# Revit family: VIESSMANN - Vitocrossal 200 CM2C
name_source: partatom
category: Wyposażenie mechaniczne
revit_build: Autodesk Revit 2017 (Build: 20160720_1515(x64)
units: mm (PartAtom-declared; Revit-internal decimal feet)

## family parameters
Numer OmniClass = 23.15.30.27.21
Oparty na płaszczyźnie roboczej = Nie
Punkt obliczania pomieszczeń = Nie
Tnij formami wycięć po wczytaniu = Tak
Typ części = Normalny
Tytuł OmniClass = Gas Tanks and Gasholders
Współdzielony = Nie
Wymiar okrągłego złącza = Użyj średnicy
Zawsze pionowo = Tak

## types (7) — shared parameters
Autor = https://www.archispace.pl
Ciśnienie kontrolne = 0.8 MPa
Ciśnienie na przyłączu gazu - gaz płynny = 5 - 5.75 kPa
Ciśnienie na przyłączu gazu - gaz ziemny = 2 - 5 kPa
Częstotliwość = 50 Hz
Dop. maks. ciśnienie robocze = 0.6 MPa
Dop. min. ciśnienie robocze = 0.1 MPa
Dop. temperatura na zasilaniu (=temperatura progowa) = 110 °C
Dop. temperatura robocza = 95 °C
Długość = 1755 mm  [stored 5.75787 ft]
Długość fundamentu = 1200 mm
Długość palnika = 435 mm  [stored 1.42717 ft]
Liczba biegunów = 1
NOx = Klasa 6, <56 mg/kWh
Napięcie zasilania = 230 V
Numer identyfikacyjny produktu = CE-0085CR0391
Odsunięcie króćca powrotu do kotła = 280 mm  [stored 0.918635 ft]
Opis = Gazowy kocioł grzewczy
Opis indeksowy = CE-0085CR0391
Opory przepływu = 0.0 MPa
PN 6 DN - Przyłącze zabezpieczające = 50.00 mm
Parametry produktu wg. EnEV - sprawność znormalizowana przy temperaturze w systemie grzewczym wyn. 40/30°C = do 98 (Hs)
Parametry produktu wg. EnEV - sprawność znormalizowana przy temperaturze w systemie grzewczym wyn. 75/60°C = do 96 (Hs)
Parametry spalin - dyspozycyjne ciśnienie tłoczenia na króćcu spalin = 0.0 MPa
Parametry spalin - przy obciążeniu częściowym (przy temp. wody na powrocie wyn. 30°C) = 35 °C
Parametry spalin - przy znamionowej mocy cieplnej (przy temp. wody na powrocie wyn. 30°C) = 45 °C
Parametry spalin - przy znamionowej mocy cieplnej (przy temp. wody na powrocie wyn. 60°C) = 75 °C
Producent = Viessmann Sp.z.o.o.
Przyłącze powietrza do spalania z zewnątrz (opcja dodatkowa) = 80 mm  [stored 0.262467 ft]
Spust = 1"
Syfon z odpływem kondensatu = 20.00 mm
Szerokość fundamentu = 800 mm  [stored 2.62467 ft]
Szerokość palnika = 546 mm  [stored 1.79134 ft]
Typ palnika = CM2C
URL = https://www.viessmann-projektant.pl
Viessmann Kolor 1 = Viessmann Kolor 1
Viessmann Kolor 2 = Viessmann Kolor 2
Viessmann Kolor 3 = Viessmann Kolor 3
Współczynnik mocy = 1
Wykonanie palnika = Wbudowany Modulowany
Wysokość fundamentu = 100 mm  [stored 0.328084 ft]
Zawór bezpieczeństwa (gwint zewnętrzny) = 1 1/4"

## per-type parameters (varying)
- CM2C 87kW: Długość całkowita palnika=623 mm  [stored 2.04396 ft]; Długość podstawy=1073 mm  [stored 3.52034 ft]; Masa - palnik z armaturą uniwersalną i pokrywą palnika=35.70 kg; Masa całkowita=348.00 kg; Masa znamionowa (=zezwolenie)=202.00 kg; Moc cieplna palnika dolna=27 kW; Moc cieplna palnika górna=82 kW; Moc nominalna=87 kW; Model=Gazowy kocioł kondensacyjny Viessmann Vitocrossal CM2C 87kW / Gas condensing boiler Viessmann Vitocrossal CM2C 87kW; Odsunięcie króćca przyłącza zabezpieczającego=537 mm  [stored 1.76181 ft]; Odsunięcie króćca zasilania z kotła=737 mm  [stored 2.41798 ft]; Odsunięcie podstawy=455 mm; PN 6 DN - powrót do kotła=50 mm  [stored 0.164042 ft]; PN 6 DN - zasilanie z kotła=50 mm  [stored 0.164042 ft]; Parametry spalin - masowe natężenie przepływu w przypadku gazu ziemnego przy obciążeniu częściowym=42 kg/h; Parametry spalin - masowe natężenie przepływu w przypadku gazu ziemnego przy znamionowej mocy cieplnej=126 kg/h; Pobór mocy elektrycznej - przy dolnej mocy cieplnej=23 W; Pobór mocy elektrycznej - przy górnej mocy cieplnej=75 W; Pojemność wodna kotła=225.0 L; Przepływ maksymalny=3.76 m³/h; Przyłącze gazu=1"; Przyłącze spalin=160 mm  [stored 0.524934 ft]; Straty energii dyżurnej qB,70=0.6 %; Szerokość=810 mm  [stored 2.65748 ft]; Szerokość podstawy=660 mm  [stored 2.16535 ft]; Wartości na przyłączu (w odniesieniu do maks. obciążenia) - gaz ziemny GZ-50/G20=2.8 - 8.7 m3/h; Wartości na przyłączu (w odniesieniu do maks. obciążenia) - gaz ziemny GZ41,5/G27=3.3 - 10.1 m3/h; Wysokość=1114 mm  [stored 3.65486 ft]; Wysokość do króćców=1178 mm; Wysokość króćca spalin=539 mm  [stored 1.76837 ft]; Wysokość palnika=514 mm  [stored 1.68635 ft]; Występ króćca spalin=19 mm  [stored 0.062336 ft]; Zakres znamionowej mocy cieplnej przy Tv/Tr 50/30°C=29 - 87; Zakres znamionowej mocy cieplnej przy Tv/Tr 80/60°C=26 - 80; Znamionowe obciążenie cieplne=82 kW
- CM2C 115kW: Długość całkowita palnika=623 mm  [stored 2.04396 ft]; Długość podstawy=1073 mm  [stored 3.52034 ft]; Masa - palnik z armaturą uniwersalną i pokrywą palnika=41.00 kg; Masa całkowita=350.00 kg; Masa znamionowa (=zezwolenie)=204.00 kg; Moc cieplna palnika dolna=36 kW; Moc cieplna palnika górna=109 kW; Moc nominalna=115 kW; Model=Gazowy kocioł kondensacyjny Viessmann Vitocrossal CM2C 115kW / Gas condensing boiler Viessmann Vitocrossal CM2C 115kW; Odsunięcie króćca przyłącza zabezpieczającego=537 mm  [stored 1.76181 ft]; Odsunięcie króćca zasilania z kotła=737 mm  [stored 2.41798 ft]; Odsunięcie podstawy=455 mm; PN 6 DN - powrót do kotła=50 mm  [stored 0.164042 ft]; PN 6 DN - zasilanie z kotła=50 mm  [stored 0.164042 ft]; Parametry spalin - masowe natężenie przepływu w przypadku gazu ziemnego przy obciążeniu częściowym=56 kg/h; Parametry spalin - masowe natężenie przepływu w przypadku gazu ziemnego przy znamionowej mocy cieplnej=166 kg/h; Pobór mocy elektrycznej - przy dolnej mocy cieplnej=43 W; Pobór mocy elektrycznej - przy górnej mocy cieplnej=140 W; Pojemność wodna kotła=225.0 L; Przepływ maksymalny=4.97 m³/h; Przyłącze gazu=1"; Przyłącze spalin=160 mm  [stored 0.524934 ft]; Straty energii dyżurnej qB,70=0.5 %; Szerokość=810 mm  [stored 2.65748 ft]; Szerokość podstawy=660 mm  [stored 2.16535 ft]; Wartości na przyłączu (w odniesieniu do maks. obciążenia) - gaz ziemny GZ-50/G20=3.8 - 11.5 m3/h; Wartości na przyłączu (w odniesieniu do maks. obciążenia) - gaz ziemny GZ41,5/G27=4.4 - 13.3 m3/h; Wysokość=1114 mm  [stored 3.65486 ft]; Wysokość do króćców=1178 mm; Wysokość króćca spalin=539 mm  [stored 1.76837 ft]; Wysokość palnika=514 mm  [stored 1.68635 ft]; Występ króćca spalin=19 mm  [stored 0.062336 ft]; Zakres znamionowej mocy cieplnej przy Tv/Tr 50/30°C=38 - 115; Zakres znamionowej mocy cieplnej przy Tv/Tr 80/60°C=35 - 105; Znamionowe obciążenie cieplne=109 kW
- CM2C 142kW: Długość całkowita palnika=623 mm  [stored 2.04396 ft]; Długość podstawy=1073 mm  [stored 3.52034 ft]; Masa - palnik z armaturą uniwersalną i pokrywą palnika=41.00 kg; Masa całkowita=351.00 kg; Masa znamionowa (=zezwolenie)=205.00 kg; Moc cieplna palnika dolna=45 kW; Moc cieplna palnika górna=134 kW; Moc nominalna=142 kW; Model=Gazowy kocioł kondensacyjny Viessmann Vitocrossal CM2C 142kW / Gas condensing boiler Viessmann Vitocrossal CM2C 142kW; Odsunięcie króćca przyłącza zabezpieczającego=537 mm  [stored 1.76181 ft]; Odsunięcie króćca zasilania z kotła=737 mm  [stored 2.41798 ft]; Odsunięcie podstawy=455 mm; PN 6 DN - powrót do kotła=50 mm  [stored 0.164042 ft]; PN 6 DN - zasilanie z kotła=50 mm  [stored 0.164042 ft]; Parametry spalin - masowe natężenie przepływu w przypadku gazu ziemnego przy obciążeniu częściowym=69 kg/h; Parametry spalin - masowe natężenie przepływu w przypadku gazu ziemnego przy znamionowej mocy cieplnej=207 kg/h; Pobór mocy elektrycznej - przy dolnej mocy cieplnej=50 W; Pobór mocy elektrycznej - przy górnej mocy cieplnej=210 W; Pojemność wodna kotła=221.0 L; Przepływ maksymalny=6.13 m³/h; Przyłącze gazu=1"; Przyłącze spalin=160 mm  [stored 0.524934 ft]; Straty energii dyżurnej qB,70=0.4 %; Szerokość=810 mm  [stored 2.65748 ft]; Szerokość podstawy=660 mm  [stored 2.16535 ft]; Wartości na przyłączu (w odniesieniu do maks. obciążenia) - gaz ziemny GZ-50/G20=4.7 - 14.2 m3/h; Wartości na przyłączu (w odniesieniu do maks. obciążenia) - gaz ziemny GZ41,5/G27=5.5 - 16.5 m3/h; Wysokość=1114 mm  [stored 3.65486 ft]; Wysokość do króćców=1178 mm; Wysokość króćca spalin=539 mm  [stored 1.76837 ft]; Wysokość palnika=514 mm  [stored 1.68635 ft]; Występ króćca spalin=19 mm  [stored 0.062336 ft]; Zakres znamionowej mocy cieplnej przy Tv/Tr 50/30°C=47 - 142; Zakres znamionowej mocy cieplnej przy Tv/Tr 80/60°C=43 - 130; Znamionowe obciążenie cieplne=134 kW
- CM2C 75kW: Długość całkowita palnika=623 mm  [stored 2.04396 ft]; Długość podstawy=1073 mm  [stored 3.52034 ft]; Masa - palnik z armaturą uniwersalną i pokrywą palnika=35.70 kg; Masa całkowita=348.00 kg; Masa znamionowa (=zezwolenie)=202.00 kg; Moc cieplna palnika dolna=27 kW; Moc cieplna palnika górna=71 kW; Moc nominalna=75 kW; Model=Gazowy kocioł kondensacyjny Viessmann Vitocrossal CM2C 75kW / Gas condensing boiler Viessmann Vitocrossal CM2C 75kW; Odsunięcie króćca przyłącza zabezpieczającego=537 mm  [stored 1.76181 ft]; Odsunięcie króćca zasilania z kotła=737 mm  [stored 2.41798 ft]; Odsunięcie podstawy=455 mm; PN 6 DN - powrót do kotła=50 mm  [stored 0.164042 ft]; PN 6 DN - zasilanie z kotła=50 mm  [stored 0.164042 ft]; Parametry spalin - masowe natężenie przepływu w przypadku gazu ziemnego przy obciążeniu częściowym=42 kg/h; Parametry spalin - masowe natężenie przepływu w przypadku gazu ziemnego przy znamionowej mocy cieplnej=109 kg/h; Pobór mocy elektrycznej - przy dolnej mocy cieplnej=23 W; Pobór mocy elektrycznej - przy górnej mocy cieplnej=53 W; Pojemność wodna kotła=225.0 L; Przepływ maksymalny=3.24 m³/h; Przyłącze gazu=1"; Przyłącze spalin=160 mm  [stored 0.524934 ft]; Straty energii dyżurnej qB,70=0.6 %; Szerokość=810 mm  [stored 2.65748 ft]; Szerokość podstawy=660 mm  [stored 2.16535 ft]; Wartości na przyłączu (w odniesieniu do maks. obciążenia) - gaz ziemny GZ-50/G20=3.8 - 7.5 m3/h; Wartości na przyłączu (w odniesieniu do maks. obciążenia) - gaz ziemny GZ41,5/G27=3.3 - 8.7 m3/h; Wysokość=1114 mm  [stored 3.65486 ft]; Wysokość do króćców=1178 mm; Wysokość króćca spalin=539 mm  [stored 1.76837 ft]; Wysokość palnika=514 mm  [stored 1.68635 ft]; Występ króćca spalin=19 mm  [stored 0.062336 ft]; Zakres znamionowej mocy cieplnej przy Tv/Tr 50/30°C=30 - 75; Zakres znamionowej mocy cieplnej przy Tv/Tr 80/60°C=28 - 69; Znamionowe obciążenie cieplne=71 kW
- CM2C 186kW: Długość całkowita palnika=660 mm  [stored 2.16535 ft]; Długość podstawy=1072 mm; Masa - palnik z armaturą uniwersalną i pokrywą palnika=38.80 kg; Masa całkowita=397.00 kg; Masa znamionowa (=zezwolenie)=248.00 kg; Moc cieplna palnika dolna=35 kW; Moc cieplna palnika górna=176 kW; Moc nominalna=186 kW; Model=Gazowy kocioł kondensacyjny Viessmann Vitocrossal CM2C 186kW / Gas condensing boiler Viessmann Vitocrossal CM2C 186kW; Odsunięcie króćca przyłącza zabezpieczającego=534 mm  [stored 1.75197 ft]; Odsunięcie króćca zasilania z kotła=738 mm; Odsunięcie podstawy=437 mm  [stored 1.43373 ft]; PN 6 DN - powrót do kotła=65 mm  [stored 0.213255 ft]; PN 6 DN - zasilanie z kotła=65 mm  [stored 0.213255 ft]; Parametry spalin - masowe natężenie przepływu w przypadku gazu płynnego przy obciążeniu częściowym=54 kg/h; Parametry spalin - masowe natężenie przepływu w przypadku gazu płynnego przy znamionowej mocy cieplnej=271 kg/h; Parametry spalin - masowe natężenie przepływu w przypadku gazu ziemnego przy obciążeniu częściowym=54 kg/h; Parametry spalin - masowe natężenie przepływu w przypadku gazu ziemnego przy znamionowej mocy cieplnej=269 kg/h; Pobór mocy elektrycznej - przy dolnej mocy cieplnej=37 W; Pobór mocy elektrycznej - przy górnej mocy cieplnej=278 W; Pojemność wodna kotła=306.0 L; Przepływ maksymalny=8.04 m³/h; Przyłącze gazu=1"; Przyłącze spalin=200 mm  [stored 0.656168 ft]; Straty energii dyżurnej qB,70=0.4 %; Szerokość=910 mm; Szerokość podstawy=760 mm; Wartości na przyłączu (w odniesieniu do maks. obciążenia) - gaz płynny P/G31=2.7 - 13.6 m3/h; Wartości na przyłączu (w odniesieniu do maks. obciążenia) - gaz ziemny GZ-50/G20=3.7 - 18.6 m3/h; Wartości na przyłączu (w odniesieniu do maks. obciążenia) - gaz ziemny GZ41,5/G27=4.6 - 21.5 m3/h; Wysokość=1213 mm  [stored 3.97966 ft]; Wysokość do króćców=1277 mm  [stored 4.18963 ft]; Wysokość króćca spalin=588 mm  [stored 1.92913 ft]; Wysokość palnika=514 mm  [stored 1.68635 ft]; Występ króćca spalin=38 mm  [stored 0.124672 ft]; Zakres znamionowej mocy cieplnej przy Tv/Tr 50/30°C=37 - 186; Zakres znamionowej mocy cieplnej przy Tv/Tr 80/60°C=34 - 170; Znamionowe obciążenie cieplne=176 kW
- CM2C 246kW: Długość całkowita palnika=703 mm  [stored 2.30643 ft]; Długość podstawy=1072 mm; Masa - palnik z armaturą uniwersalną i pokrywą palnika=41.80 kg; Masa całkowita=409.00 kg; Masa znamionowa (=zezwolenie)=260.00 kg; Moc cieplna palnika dolna=58 kW; Moc cieplna palnika górna=232 kW; Moc nominalna=246 kW; Model=Gazowy kocioł kondensacyjny Viessmann Vitocrossal CM2C 246kW / Gas condensing boiler Viessmann Vitocrossal CM2C 246kW; Odsunięcie króćca przyłącza zabezpieczającego=534 mm  [stored 1.75197 ft]; Odsunięcie króćca zasilania z kotła=738 mm; Odsunięcie podstawy=437 mm  [stored 1.43373 ft]; PN 6 DN - powrót do kotła=65 mm  [stored 0.213255 ft]; PN 6 DN - zasilanie z kotła=65 mm  [stored 0.213255 ft]; Parametry spalin - masowe natężenie przepływu w przypadku gazu płynnego przy obciążeniu częściowym=90 kg/h; Parametry spalin - masowe natężenie przepływu w przypadku gazu płynnego przy znamionowej mocy cieplnej=360 kg/h; Parametry spalin - masowe natężenie przepływu w przypadku gazu ziemnego przy obciążeniu częściowym=89 kg/h; Parametry spalin - masowe natężenie przepływu w przypadku gazu ziemnego przy znamionowej mocy cieplnej=358 kg/h; Pobór mocy elektrycznej - przy dolnej mocy cieplnej=40 W; Pobór mocy elektrycznej - przy górnej mocy cieplnej=280 W; Pojemność wodna kotła=292.0 L; Przepływ maksymalny=10.63 m³/h; Przyłącze gazu=1 1/4"; Przyłącze spalin=200 mm  [stored 0.656168 ft]; Straty energii dyżurnej qB,70=0.3 %; Szerokość=910 mm; Szerokość podstawy=760 mm; Wartości na przyłączu (w odniesieniu do maks. obciążenia) - gaz płynny P/G31=4.5 - 18.0 m3/h; Wartości na przyłączu (w odniesieniu do maks. obciążenia) - gaz ziemny GZ-50/G20=6.1 - 24.6 m3/h; Wartości na przyłączu (w odniesieniu do maks. obciążenia) - gaz ziemny GZ41,5/G27=7.1 - 28.6 m3/h; Wysokość=1213 mm  [stored 3.97966 ft]; Wysokość do króćców=1277 mm  [stored 4.18963 ft]; Wysokość króćca spalin=588 mm  [stored 1.92913 ft]; Wysokość palnika=534 mm  [stored 1.75197 ft]; Występ króćca spalin=38 mm  [stored 0.124672 ft]; Zakres znamionowej mocy cieplnej przy Tv/Tr 50/30°C=62 - 246; Zakres znamionowej mocy cieplnej przy Tv/Tr 80/60°C=56 - 225; Znamionowe obciążenie cieplne=232 kW
- CM2C 311kW: Długość całkowita palnika=703 mm  [stored 2.30643 ft]; Długość podstawy=1072 mm; Masa - palnik z armaturą uniwersalną i pokrywą palnika=41.80 kg; Masa całkowita=422.00 kg; Masa znamionowa (=zezwolenie)=273.00 kg; Moc cieplna palnika dolna=59 kW; Moc cieplna palnika górna=293 kW; Moc nominalna=311 kW; Model=Gazowy kocioł kondensacyjny Viessmann Vitocrossal CM2C 311kW / Gas condensing boiler Viessmann Vitocrossal CM2C 311kW; Odsunięcie króćca przyłącza zabezpieczającego=534 mm  [stored 1.75197 ft]; Odsunięcie króćca zasilania z kotła=738 mm; Odsunięcie podstawy=437 mm  [stored 1.43373 ft]; PN 6 DN - powrót do kotła=65 mm  [stored 0.213255 ft]; PN 6 DN - zasilanie z kotła=65 mm  [stored 0.213255 ft]; Parametry spalin - masowe natężenie przepływu w przypadku gazu płynnego przy obciążeniu częściowym=92 kg/h; Parametry spalin - masowe natężenie przepływu w przypadku gazu płynnego przy znamionowej mocy cieplnej=454 kg/h; Parametry spalin - masowe natężenie przepływu w przypadku gazu ziemnego przy obciążeniu częściowym=91 kg/h; Parametry spalin - masowe natężenie przepływu w przypadku gazu ziemnego przy znamionowej mocy cieplnej=452 kg/h; Pobór mocy elektrycznej - przy dolnej mocy cieplnej=47 W; Pobór mocy elektrycznej - przy górnej mocy cieplnej=378 W; Pojemność wodna kotła=279.0 L; Przepływ maksymalny=13.44 m³/h; Przyłącze gazu=1 1/4"; Przyłącze spalin=200 mm  [stored 0.656168 ft]; Straty energii dyżurnej qB,70=0.3 %; Szerokość=910 mm; Szerokość podstawy=760 mm; Wartości na przyłączu (w odniesieniu do maks. obciążenia) - gaz płynny P/G31=4.6 - 22.8 m3/h; Wartości na przyłączu (w odniesieniu do maks. obciążenia) - gaz ziemny GZ-50/G20=6.3 - 31.0 m3/h; Wartości na przyłączu (w odniesieniu do maks. obciążenia) - gaz ziemny GZ41,5/G27=7.3 - 36.1 m3/h; Wysokość=1213 mm  [stored 3.97966 ft]; Wysokość do króćców=1277 mm  [stored 4.18963 ft]; Wysokość króćca spalin=588 mm  [stored 1.92913 ft]; Wysokość palnika=534 mm  [stored 1.75197 ft]; Występ króćca spalin=38 mm  [stored 0.124672 ft]; Zakres znamionowej mocy cieplnej przy Tv/Tr 50/30°C=62 - 311; Zakres znamionowej mocy cieplnej przy Tv/Tr 80/60°C=57 - 285; Znamionowe obciążenie cieplne=293 kW

note: [stored X ft] marks values corroborated as IEEE doubles in the binary element streams (Revit-internal decimal feet)
